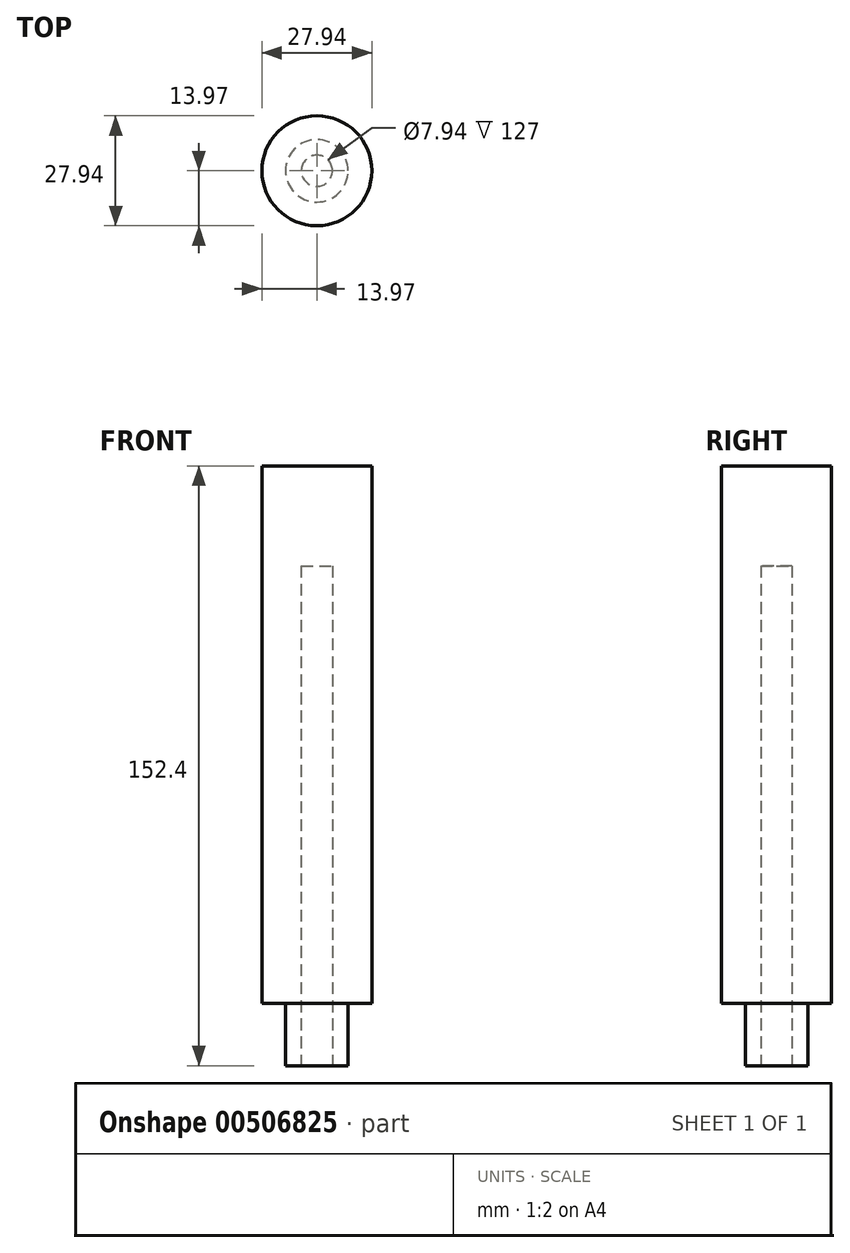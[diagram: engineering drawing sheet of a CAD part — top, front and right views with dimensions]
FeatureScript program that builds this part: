
annotation { "Feature Type Name" : "Feature", "Feature Type Description" : "" }
export const myFeature = defineFeature(function(context is Context, id is Id, definition is map)
    precondition{}
    {
        {
            var Q0;
            Q0=qCreatedBy(makeId("Top.planeOp"),FACE);
            var sketch = newSketch(context, id + "F0", { "sketchPlane" : qUnion([Q0])});
            skCircle(sketch, "E0", {"center": v(0, 0) * mm, "radius": 13.97 * mm});
            skSolve(sketch);
        }
        {
            var Q0;
            Q0 = qSketchRegion(id + "F0", true);
            extrude(context, id + "F1", {"entities" : qUnion([Q0]), "depth" : 152.4 * mm});
        }
        {
            var Q0;
            Q0=makeQuery(id+"F1.opExtrude","CAP_FACE",FACE,{"disambiguationData":[OSD([sQuery(id+"F0.wireOp",EDGE,"E0")])],"isStart":true});
            var sketch = newSketch(context, id + "F2", { "sketchPlane" : qUnion([Q0])});
            skCircle(sketch, "E1", {"center": v(0, 0) * mm, "radius": 7.94 * mm});
            skSolve(sketch);
        }
        {
            var Q0;
            Q0=makeQuery(id+"F2.imprint","IMPRINT",FACE,{"disambiguationData":[TD([[makeQuery(id+"F2.imprint","IMPRINT",EDGE,{"derivedFrom":sQuery(id+"F2.wireOp",EDGE,"E1")}),-1.0]])]});
            extrude(context, id + "F3", {"entities" : qUnion([Q0]), "operationType" : NewBodyOperationType.REMOVE, "oppositeDirection" : true, "depth" : 15.88 * mm});
        }
        {
            var Q0;
            Q0=makeQuery(id+"F1.opExtrude","CAP_FACE",FACE,{"disambiguationData":[OSD([sQuery(id+"F0.wireOp",EDGE,"E0")])],"isStart":true});
            var sketch = newSketch(context, id + "F4", { "sketchPlane" : qUnion([Q0])});
            skCircle(sketch, "E2", {"center": v(0, 0) * mm, "radius": 3.97 * mm});
            skSolve(sketch);
        }
        {
            var Q0;
            Q0 = qSketchRegion(id + "F4", true);
            extrude(context, id + "F5", {"entities" : qUnion([Q0]), "operationType" : NewBodyOperationType.REMOVE, "oppositeDirection" : true, "depth" : 127 * mm});
        }
    });
